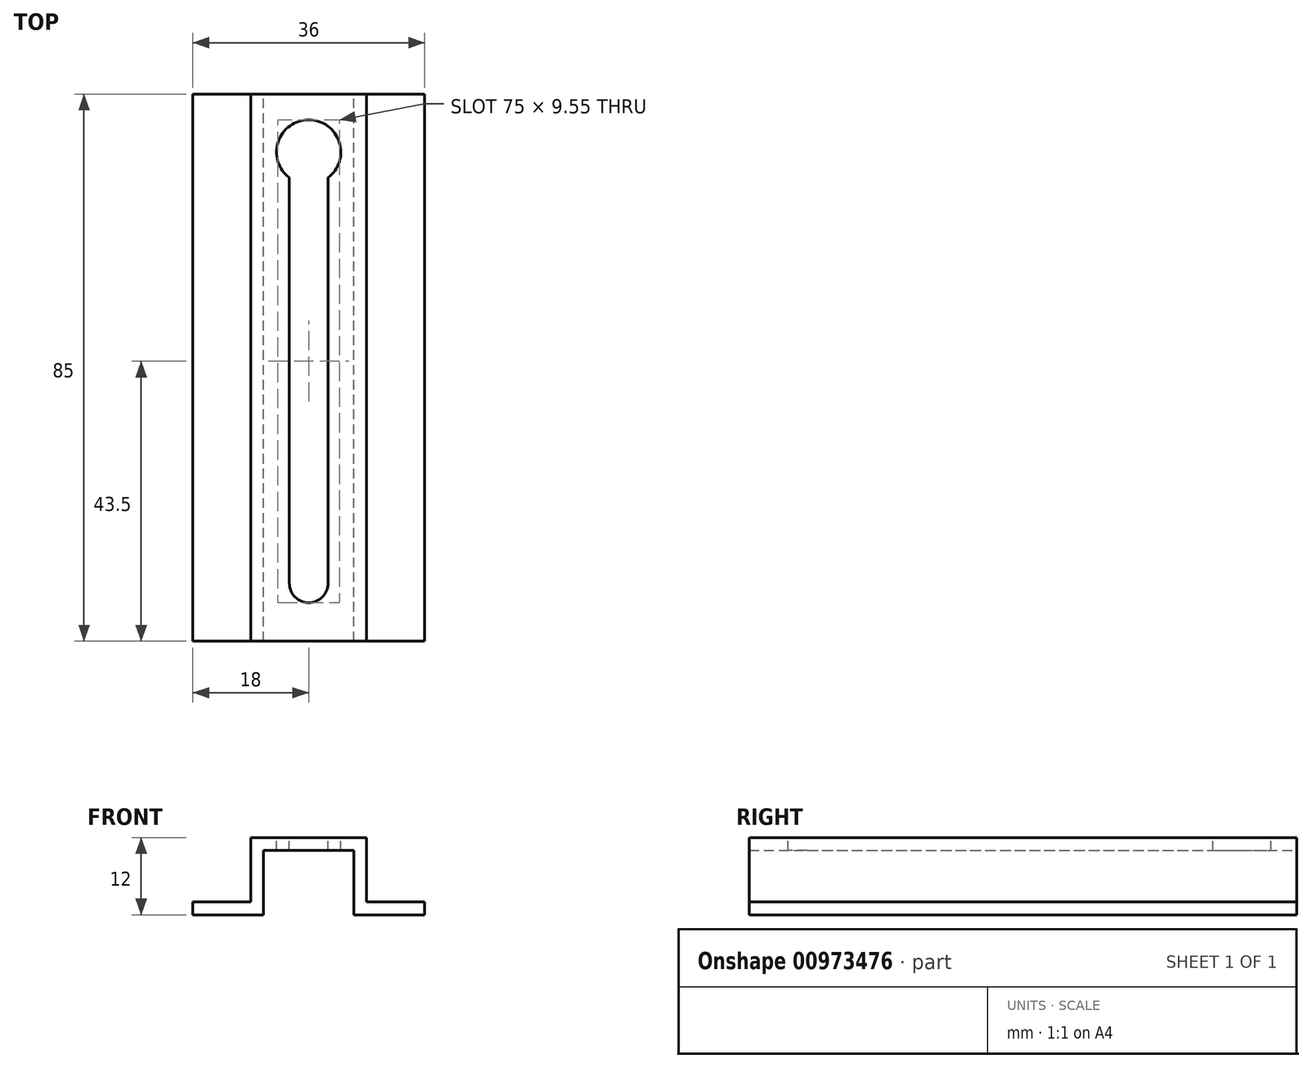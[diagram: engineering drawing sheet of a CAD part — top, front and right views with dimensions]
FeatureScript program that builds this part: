
annotation { "Feature Type Name" : "Feature", "Feature Type Description" : "" }
export const myFeature = defineFeature(function(context is Context, id is Id, definition is map)
    precondition{}
    {
        {
            var Q0;
            Q0=qCreatedBy(makeId("Top.planeOp"),FACE);
            var sketch = newSketch(context, id + "F0", { "sketchPlane" : qUnion([Q0])});
            skLineSegment(sketch, "E0.bottom", {"start": v(0, 0) * mm, "end": v(-18, 0) * mm});
            skLineSegment(sketch, "E0.top", {"start": v(0, 85) * mm, "end": v(-18, 85) * mm});
            skLineSegment(sketch, "E0.left", {"start": v(0, 0) * mm, "end": v(0, 85) * mm});
            skLineSegment(sketch, "E0.right", {"start": v(-18, 0) * mm, "end": v(-18, 85) * mm});
            skArc(sketch, "E1", {"start": v(-6, 72) * mm, "mid": v(-9, 81) * mm, "end": v(-12, 72) * mm});
            skLineSegment(sketch, "E2", {"start": v(-12, 9) * mm, "end": v(-12, 72) * mm});
            skLineSegment(sketch, "E3", {"start": v(-6, 9) * mm, "end": v(-6, 72) * mm});
            skArc(sketch, "E4", {"start": v(-12, 9) * mm, "mid": v(-9, 6) * mm, "end": v(-6, 9) * mm});
            skPoint(sketch, "E5.start.orphan", {"position": v(-9, 85) * mm});
            skSolve(sketch);
        }
        {
            var Q0;
            Q0=makeQuery(id+"F0.imprint","IMPRINT",FACE,{"disambiguationData":[TD([[makeQuery(id+"F0.imprint","IMPRINT",EDGE,{"derivedFrom":sQuery(id+"F0.wireOp",EDGE,"E0.bottom")}),-1.0]])]});
            extrude(context, id + "F1", {"entities" : qUnion([Q0]), "oppositeDirection" : true, "depth" : 2 * mm, "offsetDistance" : 25 * mm});
        }
        {
            var Q0;
            Q0=makeQuery(id+"F1.opExtrude","CAP_FACE",FACE,{"disambiguationData":[OSD([sQuery(id+"F0.wireOp",EDGE,"E0.bottom"),sQuery(id+"F0.wireOp",EDGE,"E0.top"),sQuery(id+"F0.wireOp",EDGE,"E0.left"),sQuery(id+"F0.wireOp",EDGE,"E0.right"),sQuery(id+"F0.wireOp",EDGE,"E1"),sQuery(id+"F0.wireOp",EDGE,"E2"),sQuery(id+"F0.wireOp",EDGE,"E3"),sQuery(id+"F0.wireOp",EDGE,"E4")])],"isStart":false});
            var sketch = newSketch(context, id + "F2", { "sketchPlane" : qUnion([Q0])});
            skLineSegment(sketch, "E6.bottom", {"start": v(-18, 0) * mm, "end": v(-16, 0) * mm});
            skLineSegment(sketch, "E6.top", {"start": v(-18, -85) * mm, "end": v(-16, -85) * mm});
            skLineSegment(sketch, "E6.left", {"start": v(-18, 0) * mm, "end": v(-18, -85) * mm});
            skLineSegment(sketch, "E6.right", {"start": v(-16, 0) * mm, "end": v(-16, -85) * mm});
            skLineSegment(sketch, "E7.bottom", {"start": v(0, 0) * mm, "end": v(-2, 0) * mm});
            skLineSegment(sketch, "E7.top", {"start": v(0, -85) * mm, "end": v(-2, -85) * mm});
            skLineSegment(sketch, "E7.left", {"start": v(0, 0) * mm, "end": v(0, -85) * mm});
            skLineSegment(sketch, "E7.right", {"start": v(-2, 0) * mm, "end": v(-2, -85) * mm});
            skSolve(sketch);
        }
        {
            var Q0;
            Q0=makeQuery(id+"F2.imprint","IMPRINT",FACE,{"disambiguationData":[TD([[makeQuery(id+"F2.imprint","IMPRINT",EDGE,{"derivedFrom":sQuery(id+"F2.wireOp",EDGE,"E7.bottom")}),1.0]])]});
            var Q1;
            Q1=makeQuery(id+"F2.imprint","IMPRINT",FACE,{"disambiguationData":[TD([[makeQuery(id+"F2.imprint","IMPRINT",EDGE,{"derivedFrom":sQuery(id+"F2.wireOp",EDGE,"E6.bottom")}),1.0]])]});
            extrude(context, id + "F3", {"entities" : qUnion([Q0, Q1]), "operationType" : NewBodyOperationType.ADD, "depth" : 10 * mm, "offsetDistance" : 25 * mm});
        }
        {
            var Q0;
            Q0=makeQuery(id+"F3.boolean.opBoolean","MERGE",FACE,{"derivedFrom":[makeQuery(id+"F1.opExtrude","SWEPT_FACE",FACE,{"disambiguationData":[OSD([sQuery(id+"F0.wireOp",EDGE,"E0.left")])]}),makeQuery(id+"F3.opExtrude","SWEPT_FACE",FACE,{"disambiguationData":[OSD([sQuery(id+"F2.wireOp",EDGE,"E7.left")])]})]});
            var sketch = newSketch(context, id + "F4", { "sketchPlane" : qUnion([Q0])});
            skLineSegment(sketch, "E8.bottom", {"start": v(0, -12) * mm, "end": v(85, -12) * mm});
            skLineSegment(sketch, "E8.top", {"start": v(0, -10) * mm, "end": v(85, -10) * mm});
            skLineSegment(sketch, "E8.left", {"start": v(0, -12) * mm, "end": v(0, -10) * mm});
            skLineSegment(sketch, "E8.right", {"start": v(85, -12) * mm, "end": v(85, -10) * mm});
            skSolve(sketch);
        }
        {
            var Q0;
            Q0=makeQuery(id+"F4.imprint","IMPRINT",FACE,{"disambiguationData":[TD([[makeQuery(id+"F4.imprint","IMPRINT",EDGE,{"derivedFrom":sQuery(id+"F4.wireOp",EDGE,"E8.bottom")}),1.0]])]});
            extrude(context, id + "F5", {"entities" : qUnion([Q0]), "operationType" : NewBodyOperationType.ADD, "depth" : 9 * mm, "offsetDistance" : 25 * mm});
        }
        {
            var Q0;
            Q0=makeQuery(id+"F3.boolean.opBoolean","MERGE",FACE,{"derivedFrom":[makeQuery(id+"F1.opExtrude","SWEPT_FACE",FACE,{"disambiguationData":[OSD([sQuery(id+"F0.wireOp",EDGE,"E0.right")])]}),makeQuery(id+"F3.opExtrude","SWEPT_FACE",FACE,{"disambiguationData":[OSD([sQuery(id+"F2.wireOp",EDGE,"E6.left")])]})]});
            var sketch = newSketch(context, id + "F6", { "sketchPlane" : qUnion([Q0])});
            skLineSegment(sketch, "E9.bottom", {"start": v(-85, -12) * mm, "end": v(0, -12) * mm});
            skLineSegment(sketch, "E9.top", {"start": v(-85, -10) * mm, "end": v(0, -10) * mm});
            skLineSegment(sketch, "E9.left", {"start": v(-85, -12) * mm, "end": v(-85, -10) * mm});
            skLineSegment(sketch, "E9.right", {"start": v(0, -12) * mm, "end": v(0, -10) * mm});
            skSolve(sketch);
        }
        {
            var Q0;
            Q0=makeQuery(id+"F6.imprint","IMPRINT",FACE,{"disambiguationData":[TD([[makeQuery(id+"F6.imprint","IMPRINT",EDGE,{"derivedFrom":sQuery(id+"F6.wireOp",EDGE,"E9.bottom")}),-1.0]])]});
            extrude(context, id + "F7", {"entities" : qUnion([Q0]), "operationType" : NewBodyOperationType.ADD, "depth" : 9 * mm, "offsetDistance" : 25 * mm});
        }
    });
